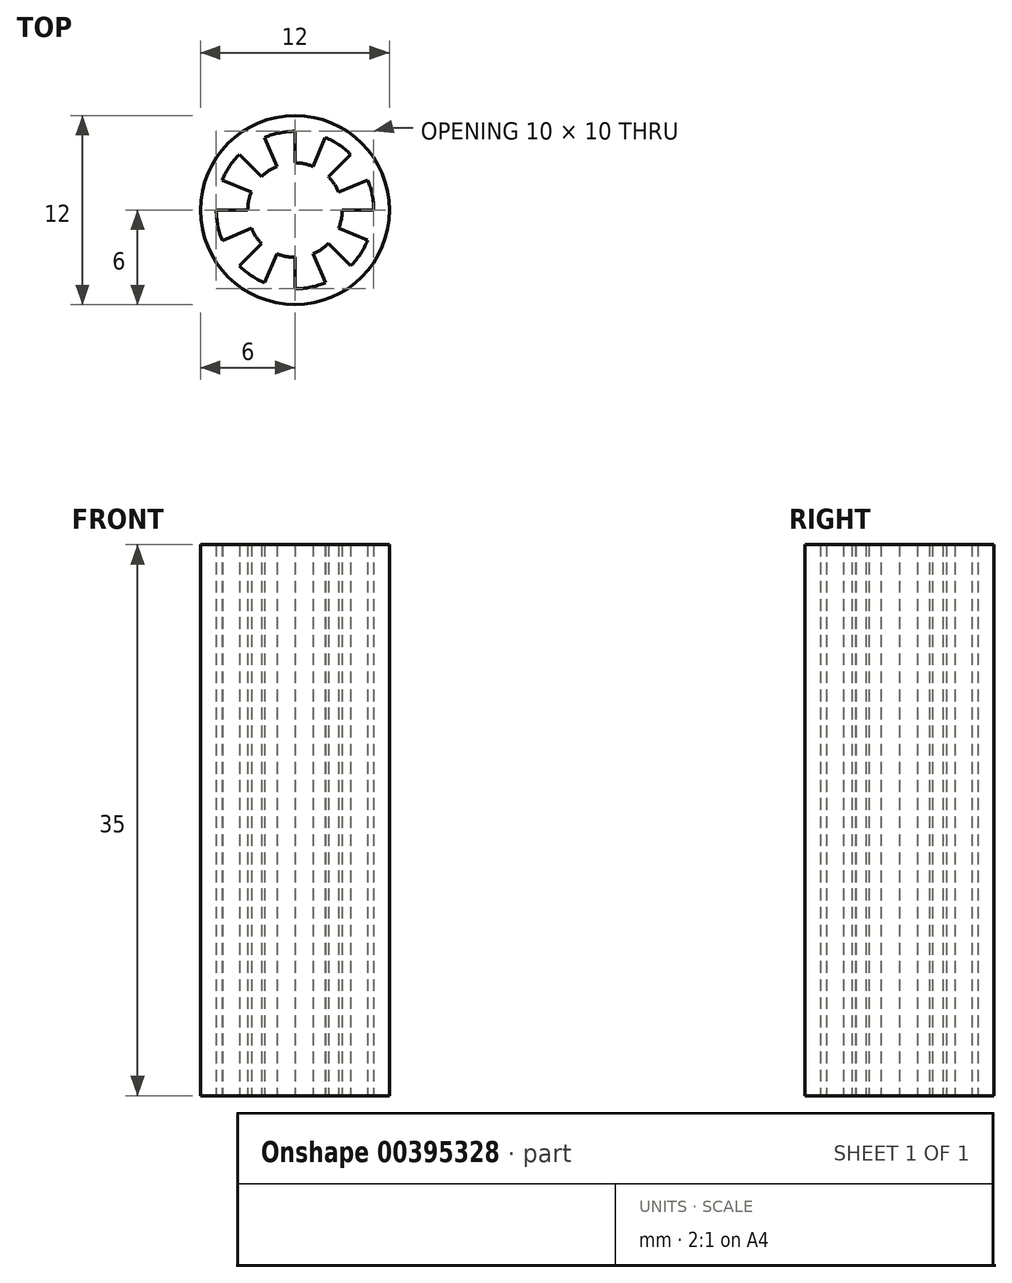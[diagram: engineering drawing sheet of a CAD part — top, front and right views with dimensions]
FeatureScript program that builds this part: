
annotation { "Feature Type Name" : "Feature", "Feature Type Description" : "" }
export const myFeature = defineFeature(function(context is Context, id is Id, definition is map)
    precondition{}
    {
        {
            var Q0;
            Q0=qCreatedBy(makeId("Top.planeOp"),FACE);
            var sketch = newSketch(context, id + "F0", { "sketchPlane" : qUnion([Q0])});
            skCircle(sketch, "E0", {"center": v(0, 0) * mm, "radius": 6 * mm});
            skCircle(sketch, "E1", {"center": v(0, 0) * mm, "radius": 5 * mm});
            skCircle(sketch, "E2", {"center": v(0, 0) * mm, "radius": 3 * mm});
            skPoint(sketch, "E3", {"position": v(0, 5) * mm});
            skPoint(sketch, "E4", {"position": v(0, -5) * mm});
            skPoint(sketch, "E5", {"position": v(5, 0) * mm});
            skPoint(sketch, "E6", {"position": v(-5, 0) * mm});
            skPoint(sketch, "E7", {"position": v(3.54, -3.54) * mm});
            skPoint(sketch, "E8", {"position": v(3.54, 3.54) * mm});
            skLineSegment(sketch, "E9", {"start": v(0, 5) * mm, "end": v(0, -5) * mm});
            skLineSegment(sketch, "E10", {"start": v(-5, 0) * mm, "end": v(5, 0) * mm});
            skPoint(sketch, "E11", {"position": v(-3.54, -3.54) * mm});
            skPoint(sketch, "E12", {"position": v(-3.54, 3.54) * mm});
            skLineSegment(sketch, "E13", {"start": v(-3.54, 3.54) * mm, "end": v(0, 0) * mm});
            skLineSegment(sketch, "E14", {"start": v(-3.54, -3.54) * mm, "end": v(0, 0) * mm});
            skLineSegment(sketch, "E15", {"start": v(0, 0) * mm, "end": v(3.54, 3.54) * mm});
            skLineSegment(sketch, "E16", {"start": v(0, 0) * mm, "end": v(3.54, -3.54) * mm});
            skPoint(sketch, "E17", {"position": v(1.92, 4.62) * mm});
            skPoint(sketch, "E18", {"position": v(4.62, 1.9) * mm});
            skPoint(sketch, "E19", {"position": v(4.62, -1.92) * mm});
            skPoint(sketch, "E20", {"position": v(1.93, -4.61) * mm});
            skPoint(sketch, "E21", {"position": v(-1.92, -4.62) * mm});
            skPoint(sketch, "E22", {"position": v(-4.61, -1.93) * mm});
            skPoint(sketch, "E23", {"position": v(-4.62, 1.92) * mm});
            skPoint(sketch, "E24", {"position": v(-1.92, 4.62) * mm});
            skLineSegment(sketch, "E25", {"start": v(1.92, 4.62) * mm, "end": v(0, 0) * mm});
            skLineSegment(sketch, "E26", {"start": v(-4.62, 1.92) * mm, "end": v(0, 0) * mm});
            skLineSegment(sketch, "E27", {"start": v(-4.61, -1.93) * mm, "end": v(0, 0) * mm});
            skLineSegment(sketch, "E28", {"start": v(-1.92, -4.62) * mm, "end": v(0, 0) * mm});
            skLineSegment(sketch, "E29", {"start": v(1.93, -4.61) * mm, "end": v(0, 0) * mm});
            skLineSegment(sketch, "E30", {"start": v(4.62, -1.92) * mm, "end": v(0, 0) * mm});
            skLineSegment(sketch, "E31", {"start": v(4.62, 1.9) * mm, "end": v(0, 0) * mm});
            skLineSegment(sketch, "E32", {"start": v(-1.92, 4.62) * mm, "end": v(0, 0) * mm});
            skSolve(sketch);
        }
        {
            var Q0;
            Q0=makeQuery(id+"F0.imprint","IMPRINT",FACE,{"disambiguationData":[TD([[makeQuery(id+"F0.imprint","IMPRINT",EDGE,{"derivedFrom":sQuery(id+"F0.wireOp",EDGE,"E0")}),1.0]])]});
            var Q1;
            {var subQ0=sQuery(id+"F0.wireOp",EDGE,"E13");var subQ1=sQuery(id+"F0.wireOp",EDGE,"E1");var subQ2=makeQuery(id+"F0.imprint","INTERSECT",VERTEX,{"derivedFrom":[subQ1,subQ0]});Q1=makeQuery(id+"F0.imprint","IMPRINT",FACE,{"disambiguationData":[TD([[makeQuery(id+"F0.imprint","IMPRINT",EDGE,{"disambiguationData":[TD([[subQ2,1.0]])],"derivedFrom":subQ1}),1.0]])]});}
            var Q2;
            {var subQ0=sQuery(id+"F0.wireOp",EDGE,"E9");var subQ1=sQuery(id+"F0.wireOp",EDGE,"E1");var subQ2=makeQuery(id+"F0.imprint","INTERSECT",VERTEX,{"disambiguationData":[OD(0.0)],"derivedFrom":[subQ1,subQ0]});Q2=makeQuery(id+"F0.imprint","IMPRINT",FACE,{"disambiguationData":[TD([[makeQuery(id+"F0.imprint","IMPRINT",EDGE,{"disambiguationData":[TD([[subQ2,1.0]])],"derivedFrom":subQ1}),1.0]])]});}
            var Q3;
            {var subQ0=sQuery(id+"F0.wireOp",EDGE,"E15");var subQ1=sQuery(id+"F0.wireOp",EDGE,"E1");var subQ2=makeQuery(id+"F0.imprint","INTERSECT",VERTEX,{"derivedFrom":[subQ1,subQ0]});Q3=makeQuery(id+"F0.imprint","IMPRINT",FACE,{"disambiguationData":[TD([[makeQuery(id+"F0.imprint","IMPRINT",EDGE,{"disambiguationData":[TD([[subQ2,1.0]])],"derivedFrom":subQ1}),1.0]])]});}
            var Q4;
            {var subQ0=sQuery(id+"F0.wireOp",EDGE,"E10");var subQ1=sQuery(id+"F0.wireOp",EDGE,"E1");var subQ2=makeQuery(id+"F0.imprint","INTERSECT",VERTEX,{"disambiguationData":[OD(1.0)],"derivedFrom":[subQ1,subQ0]});Q4=makeQuery(id+"F0.imprint","IMPRINT",FACE,{"disambiguationData":[TD([[makeQuery(id+"F0.imprint","IMPRINT",EDGE,{"disambiguationData":[TD([[subQ2,1.0]])],"derivedFrom":subQ1}),1.0]])]});}
            var Q5;
            {var subQ0=sQuery(id+"F0.wireOp",EDGE,"E16");var subQ1=sQuery(id+"F0.wireOp",EDGE,"E1");var subQ2=makeQuery(id+"F0.imprint","INTERSECT",VERTEX,{"derivedFrom":[subQ1,subQ0]});Q5=makeQuery(id+"F0.imprint","IMPRINT",FACE,{"disambiguationData":[TD([[makeQuery(id+"F0.imprint","IMPRINT",EDGE,{"disambiguationData":[TD([[subQ2,1.0]])],"derivedFrom":subQ1}),1.0]])]});}
            var Q6;
            {var subQ0=sQuery(id+"F0.wireOp",EDGE,"E9");var subQ1=sQuery(id+"F0.wireOp",EDGE,"E1");var subQ2=makeQuery(id+"F0.imprint","INTERSECT",VERTEX,{"disambiguationData":[OD(1.0)],"derivedFrom":[subQ1,subQ0]});Q6=makeQuery(id+"F0.imprint","IMPRINT",FACE,{"disambiguationData":[TD([[makeQuery(id+"F0.imprint","IMPRINT",EDGE,{"disambiguationData":[TD([[subQ2,1.0]])],"derivedFrom":subQ1}),1.0]])]});}
            var Q7;
            {var subQ0=sQuery(id+"F0.wireOp",EDGE,"E14");var subQ1=sQuery(id+"F0.wireOp",EDGE,"E1");var subQ2=makeQuery(id+"F0.imprint","INTERSECT",VERTEX,{"derivedFrom":[subQ1,subQ0]});Q7=makeQuery(id+"F0.imprint","IMPRINT",FACE,{"disambiguationData":[TD([[makeQuery(id+"F0.imprint","IMPRINT",EDGE,{"disambiguationData":[TD([[subQ2,1.0]])],"derivedFrom":subQ1}),1.0]])]});}
            var Q8;
            {var subQ0=sQuery(id+"F0.wireOp",EDGE,"E10");var subQ1=sQuery(id+"F0.wireOp",EDGE,"E1");var subQ2=makeQuery(id+"F0.imprint","INTERSECT",VERTEX,{"disambiguationData":[OD(0.0)],"derivedFrom":[subQ1,subQ0]});Q8=makeQuery(id+"F0.imprint","IMPRINT",FACE,{"disambiguationData":[TD([[makeQuery(id+"F0.imprint","IMPRINT",EDGE,{"disambiguationData":[TD([[subQ2,1.0]])],"derivedFrom":subQ1}),1.0]])]});}
            extrude(context, id + "F1", {"entities" : qUnion([Q0, Q1, Q2, Q3, Q4, Q5, Q6, Q7, Q8]), "depth" : 35 * mm});
        }
    });
